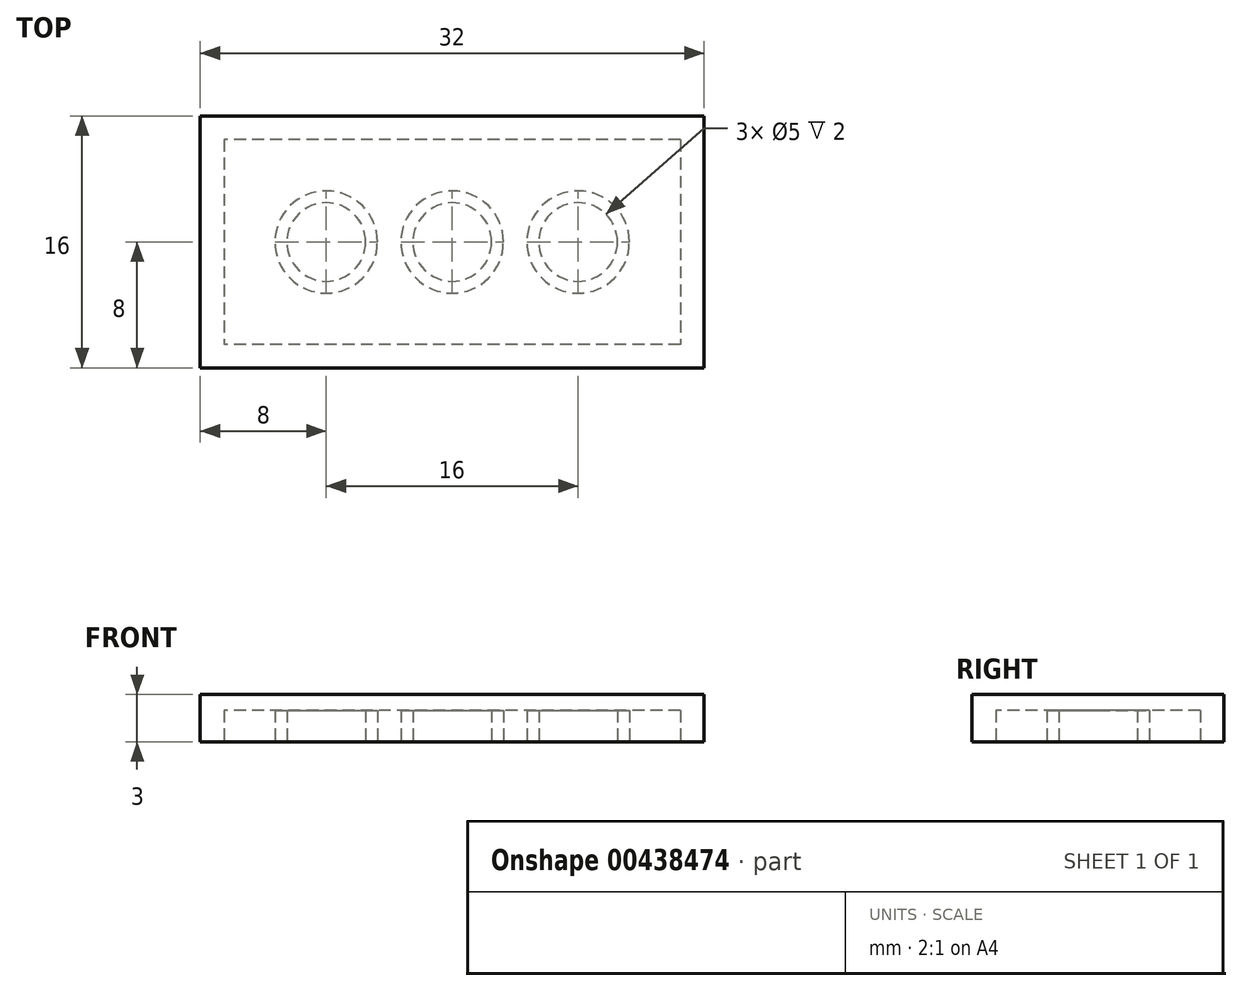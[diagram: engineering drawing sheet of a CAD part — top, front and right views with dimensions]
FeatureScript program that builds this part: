
annotation { "Feature Type Name" : "Feature", "Feature Type Description" : "" }
export const myFeature = defineFeature(function(context is Context, id is Id, definition is map)
    precondition{}
    {
        {
            var Q0;
            Q0=qCreatedBy(makeId("Top.planeOp"),FACE);
            var sketch = newSketch(context, id + "F0", { "sketchPlane" : qUnion([Q0])});
            skLineSegment(sketch, "E0.bottom", {"start": v(16, 8) * mm, "end": v(-16, 8) * mm});
            skLineSegment(sketch, "E0.top", {"start": v(16, -8) * mm, "end": v(-16, -8) * mm});
            skLineSegment(sketch, "E0.left", {"start": v(16, 8) * mm, "end": v(16, -8) * mm});
            skLineSegment(sketch, "E0.right", {"start": v(-16, 8) * mm, "end": v(-16, -8) * mm});
            skPoint(sketch, "E0.middle", {"position": v(0, 0) * mm});
            skSolve(sketch);
        }
        {
            var Q0;
            Q0=makeQuery(id+"F0.imprint","IMPRINT",FACE,{"disambiguationData":[TD([[makeQuery(id+"F0.imprint","IMPRINT",EDGE,{"derivedFrom":sQuery(id+"F0.wireOp",EDGE,"E0.bottom")}),1.0]])]});
            extrude(context, id + "F1", {"entities" : qUnion([Q0]), "depth" : 3 * mm});
        }
        {
            var Q0;
            Q0=makeQuery(id+"F1.opExtrude","CAP_FACE",FACE,{"disambiguationData":[OSD([sQuery(id+"F0.wireOp",EDGE,"E0.bottom"),sQuery(id+"F0.wireOp",EDGE,"E0.top"),sQuery(id+"F0.wireOp",EDGE,"E0.left"),sQuery(id+"F0.wireOp",EDGE,"E0.right")])],"isStart":true});
            var sketch = newSketch(context, id + "F2", { "sketchPlane" : qUnion([Q0])});
            skLineSegment(sketch, "E1.bottom", {"start": v(14.5, -6.5) * mm, "end": v(-14.5, -6.5) * mm});
            skLineSegment(sketch, "E1.top", {"start": v(14.5, 6.5) * mm, "end": v(-14.5, 6.5) * mm});
            skLineSegment(sketch, "E1.left", {"start": v(14.5, -6.5) * mm, "end": v(14.5, 6.5) * mm});
            skLineSegment(sketch, "E1.right", {"start": v(-14.5, -6.5) * mm, "end": v(-14.5, 6.5) * mm});
            skPoint(sketch, "E1.middle", {"position": v(0, 0) * mm});
            skPoint(sketch, "E1.middle.positionSnap0", {"position": v(0, 8) * mm});
            skPoint(sketch, "E1.centerSnap0", {"position": v(0, 8) * mm});
            skCircle(sketch, "E2", {"center": v(0, 0) * mm, "radius": 3.25 * mm});
            skCircle(sketch, "E3", {"center": v(0, 0) * mm, "radius": 2.5 * mm});
            skCircle(sketch, "E4.1.0.0", {"center": v(8, 0) * mm, "radius": 2.5 * mm});
            skCircle(sketch, "E4.1.0.1", {"center": v(8, 0) * mm, "radius": 3.25 * mm});
            skLineSegment(sketch, "E4.direction1", {"start": v(0, 0) * mm, "end": v(8, 0) * mm, "construction": true});
            skCircle(sketch, "E5.1.0.0", {"center": v(-8, 0) * mm, "radius": 3.25 * mm});
            skCircle(sketch, "E5.1.0.1", {"center": v(-8, 0) * mm, "radius": 2.5 * mm});
            skLineSegment(sketch, "E5.direction1", {"start": v(0, 0) * mm, "end": v(-8, 0) * mm, "construction": true});
            skSolve(sketch);
        }
        {
            var Q0;
            Q0=makeQuery(id+"F2.imprint","IMPRINT",FACE,{"disambiguationData":[TD([[makeQuery(id+"F2.imprint","IMPRINT",EDGE,{"derivedFrom":sQuery(id+"F2.wireOp",EDGE,"E1.bottom")}),-1.0]])]});
            var Q1;
            Q1=makeQuery(id+"F2.imprint","IMPRINT",FACE,{"disambiguationData":[TD([[makeQuery(id+"F2.imprint","IMPRINT",EDGE,{"derivedFrom":sQuery(id+"F2.wireOp",EDGE,"E5.1.0.1")}),1.0]])]});
            var Q2;
            Q2=makeQuery(id+"F2.imprint","IMPRINT",FACE,{"disambiguationData":[TD([[makeQuery(id+"F2.imprint","IMPRINT",EDGE,{"derivedFrom":sQuery(id+"F2.wireOp",EDGE,"E3")}),1.0]])]});
            var Q3;
            Q3=makeQuery(id+"F2.imprint","IMPRINT",FACE,{"disambiguationData":[TD([[makeQuery(id+"F2.imprint","IMPRINT",EDGE,{"derivedFrom":sQuery(id+"F2.wireOp",EDGE,"E4.1.0.0")}),1.0]])]});
            extrude(context, id + "F3", {"entities" : qUnion([Q0, Q1, Q2, Q3]), "operationType" : NewBodyOperationType.REMOVE, "oppositeDirection" : true, "depth" : 2 * mm});
        }
    });
